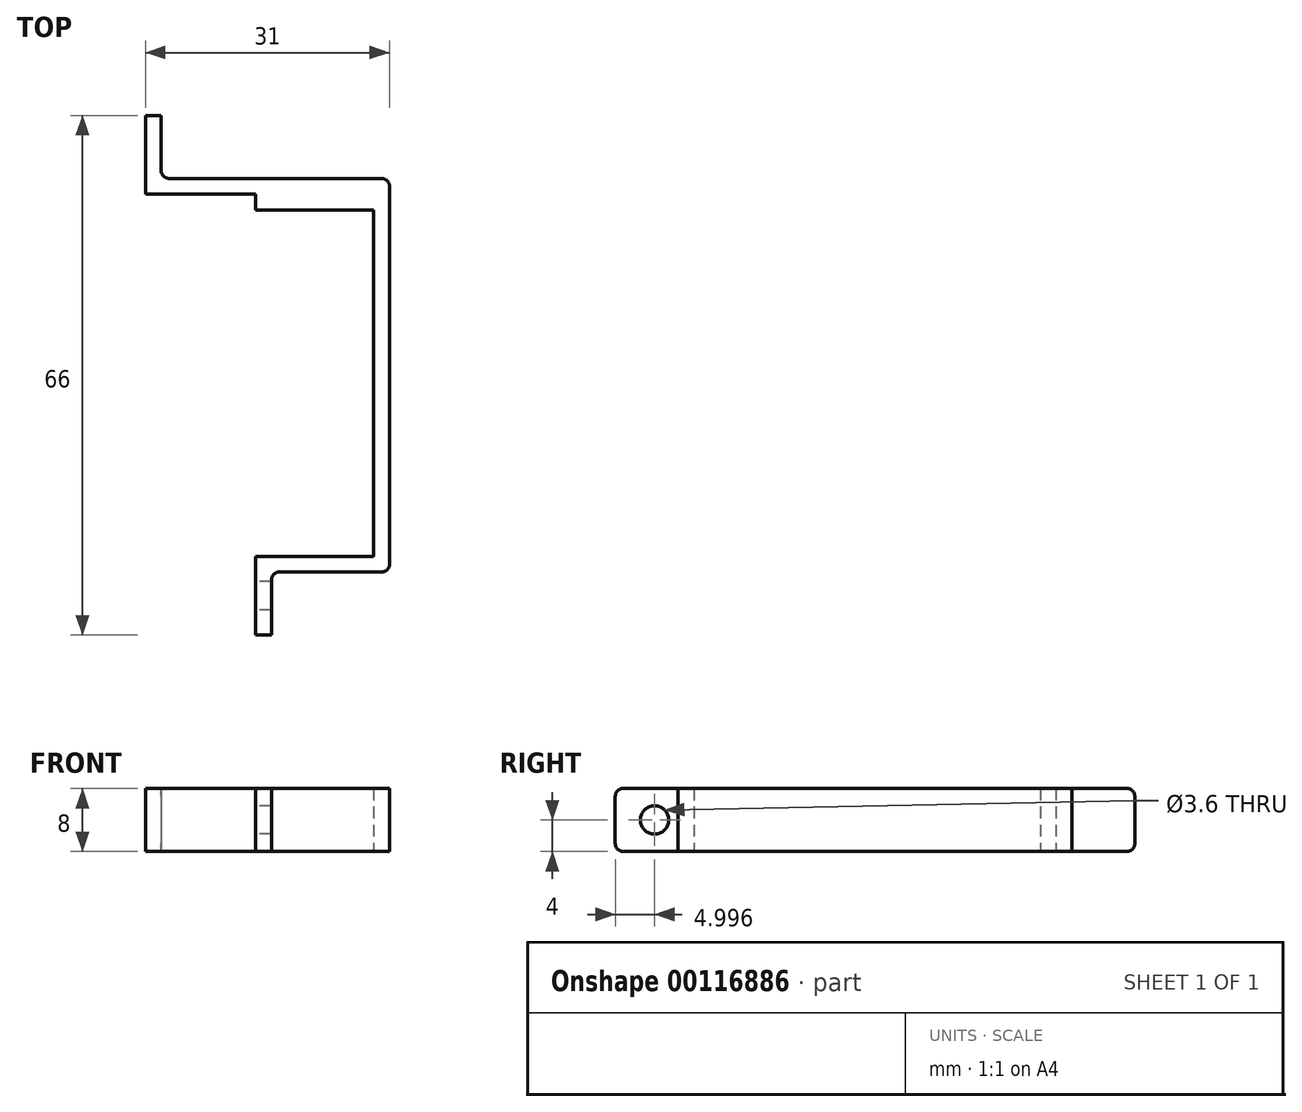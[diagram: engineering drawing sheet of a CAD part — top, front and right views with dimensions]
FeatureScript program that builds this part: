
annotation { "Feature Type Name" : "Feature", "Feature Type Description" : "" }
export const myFeature = defineFeature(function(context is Context, id is Id, definition is map)
    precondition{}
    {
        {
            var Q0;
            Q0=qCreatedBy(makeId("Top.planeOp"),FACE);
            var sketch = newSketch(context, id + "F0", { "sketchPlane" : qUnion([Q0])});
            skLineSegment(sketch, "E0", {"start": v(-25.43, -0.76) * mm, "end": v(3.57, -0.76) * mm});
            skLineSegment(sketch, "E1", {"start": v(3.57, -0.76) * mm, "end": v(3.57, -50.76) * mm});
            skLineSegment(sketch, "E2", {"start": v(3.57, -50.76) * mm, "end": v(-11.43, -50.76) * mm});
            skLineSegment(sketch, "E3", {"start": v(-11.43, -50.76) * mm, "end": v(-11.43, -58.76) * mm});
            skLineSegment(sketch, "E4", {"start": v(-11.43, -58.76) * mm, "end": v(-13.43, -58.76) * mm});
            skLineSegment(sketch, "E5", {"start": v(-13.43, -58.76) * mm, "end": v(-13.43, -48.76) * mm});
            skLineSegment(sketch, "E6", {"start": v(-13.43, -48.76) * mm, "end": v(1.57, -48.76) * mm});
            skLineSegment(sketch, "E7", {"start": v(1.57, -48.76) * mm, "end": v(1.57, -4.76) * mm});
            skLineSegment(sketch, "E8", {"start": v(1.57, -4.76) * mm, "end": v(-13.43, -4.76) * mm});
            skLineSegment(sketch, "E9", {"start": v(-27.43, -2.76) * mm, "end": v(-27.43, 7.24) * mm});
            skLineSegment(sketch, "E10", {"start": v(-27.43, 7.24) * mm, "end": v(-25.43, 7.24) * mm});
            skLineSegment(sketch, "E11", {"start": v(-25.43, 7.24) * mm, "end": v(-25.43, -0.76) * mm});
            skLineSegment(sketch, "E12", {"start": v(-13.43, -4.76) * mm, "end": v(-13.43, -2.76) * mm});
            skLineSegment(sketch, "E13", {"start": v(-13.43, -2.76) * mm, "end": v(-27.43, -2.76) * mm});
            skSolve(sketch);
        }
        {
            var Q0;
            Q0=makeQuery(id+"F0.imprint","IMPRINT",FACE,{"disambiguationData":[TD([[makeQuery(id+"F0.imprint","IMPRINT",EDGE,{"derivedFrom":sQuery(id+"F0.wireOp",EDGE,"E0")}),-1.0]])]});
            extrude(context, id + "F1", {"entities" : qUnion([Q0]), "depth" : 8 * mm});
        }
        {
            var Q0;
            Q0=makeQuery(id+"F1.opExtrude","SWEPT_FACE",FACE,{"disambiguationData":[OSD([sQuery(id+"F0.wireOp",EDGE,"E11")])]});
            var sketch = newSketch(context, id + "F2", { "sketchPlane" : qUnion([Q0])});
            skLineSegment(sketch, "E14", {"start": v(7.24, 4) * mm, "end": v(-0.76, 4) * mm, "construction": true});
            skCircle(sketch, "E15", {"center": v(3.24, 4) * mm, "radius": 1.8 * mm});
            skSolve(sketch);
        }
        {
            var Q0;
            Q0=makeQuery(id+"F1.opExtrude","SWEPT_FACE",FACE,{"disambiguationData":[OSD([sQuery(id+"F0.wireOp",EDGE,"E5")])]});
            var sketch = newSketch(context, id + "F3", { "sketchPlane" : qUnion([Q0])});
            skLineSegment(sketch, "E16", {"start": v(58.76, 4) * mm, "end": v(48.76, 4) * mm, "construction": true});
            skCircle(sketch, "E17", {"center": v(53.76, 4) * mm, "radius": 1.8 * mm});
            skSolve(sketch);
        }
        {
            var Q0;
            Q0=makeQuery(id+"F3.imprint","IMPRINT",FACE,{"disambiguationData":[TD([[makeQuery(id+"F3.imprint","IMPRINT",EDGE,{"derivedFrom":sQuery(id+"F3.wireOp",EDGE,"E17")}),1.0]])]});
            var Q1;
            Q1=makeQuery(id+"F2.imprint","IMPRINT",FACE,{"disambiguationData":[TD([[makeQuery(id+"F2.imprint","IMPRINT",EDGE,{"derivedFrom":sQuery(id+"F2.wireOp",EDGE,"E15")}),1.0]])]});
            extrude(context, id + "F4", {"entities" : qUnion([Q0, Q1]), "operationType" : NewBodyOperationType.REMOVE, "oppositeDirection" : true, "depth" : 25 * mm});
        }
        {
            var Q0;
            Q0=makeQuery(id+"F1.opExtrude","SWEPT_EDGE",EDGE,{"disambiguationData":[OSD([sQuery(id+"F0.wireOp",EDGE,"E0"),sQuery(id+"F0.wireOp",EDGE,"E11")])]});
            var Q1;
            Q1=makeQuery(id+"F1.opExtrude","SWEPT_EDGE",EDGE,{"disambiguationData":[OSD([sQuery(id+"F0.wireOp",EDGE,"E2"),sQuery(id+"F0.wireOp",EDGE,"E3")])]});
            var Q2;
            Q2=makeQuery(id+"F1.opExtrude","SWEPT_EDGE",EDGE,{"disambiguationData":[OSD([sQuery(id+"F0.wireOp",EDGE,"E1"),sQuery(id+"F0.wireOp",EDGE,"E2")])]});
            var Q3;
            Q3=makeQuery(id+"F1.opExtrude","SWEPT_EDGE",EDGE,{"disambiguationData":[OSD([sQuery(id+"F0.wireOp",EDGE,"E0"),sQuery(id+"F0.wireOp",EDGE,"E1")])]});
            fillet(context, id + "F5", {"entities" : qUnion([Q0, Q1, Q2, Q3]), "radius" : 1 * mm, "tangentPropagation" : true, "allowEdgeOverflow" : false});
        }
        {
            var Q0;
            Q0=makeQuery(id+"F1.opExtrude","CAP_EDGE",EDGE,{"disambiguationData":[OSD([sQuery(id+"F0.wireOp",EDGE,"E10")])],"isStart":false});
            var Q1;
            Q1=makeQuery(id+"F1.opExtrude","CAP_EDGE",EDGE,{"disambiguationData":[OSD([sQuery(id+"F0.wireOp",EDGE,"E10")])],"isStart":true});
            var Q2;
            Q2=makeQuery(id+"F1.opExtrude","CAP_EDGE",EDGE,{"disambiguationData":[OSD([sQuery(id+"F0.wireOp",EDGE,"E4")])],"isStart":true});
            var Q3;
            Q3=makeQuery(id+"F1.opExtrude","CAP_EDGE",EDGE,{"disambiguationData":[OSD([sQuery(id+"F0.wireOp",EDGE,"E4")])],"isStart":false});
            fillet(context, id + "F6", {"entities" : qUnion([Q0, Q1, Q2, Q3]), "radius" : 1 * mm, "tangentPropagation" : true, "allowEdgeOverflow" : false});
        }
    });
